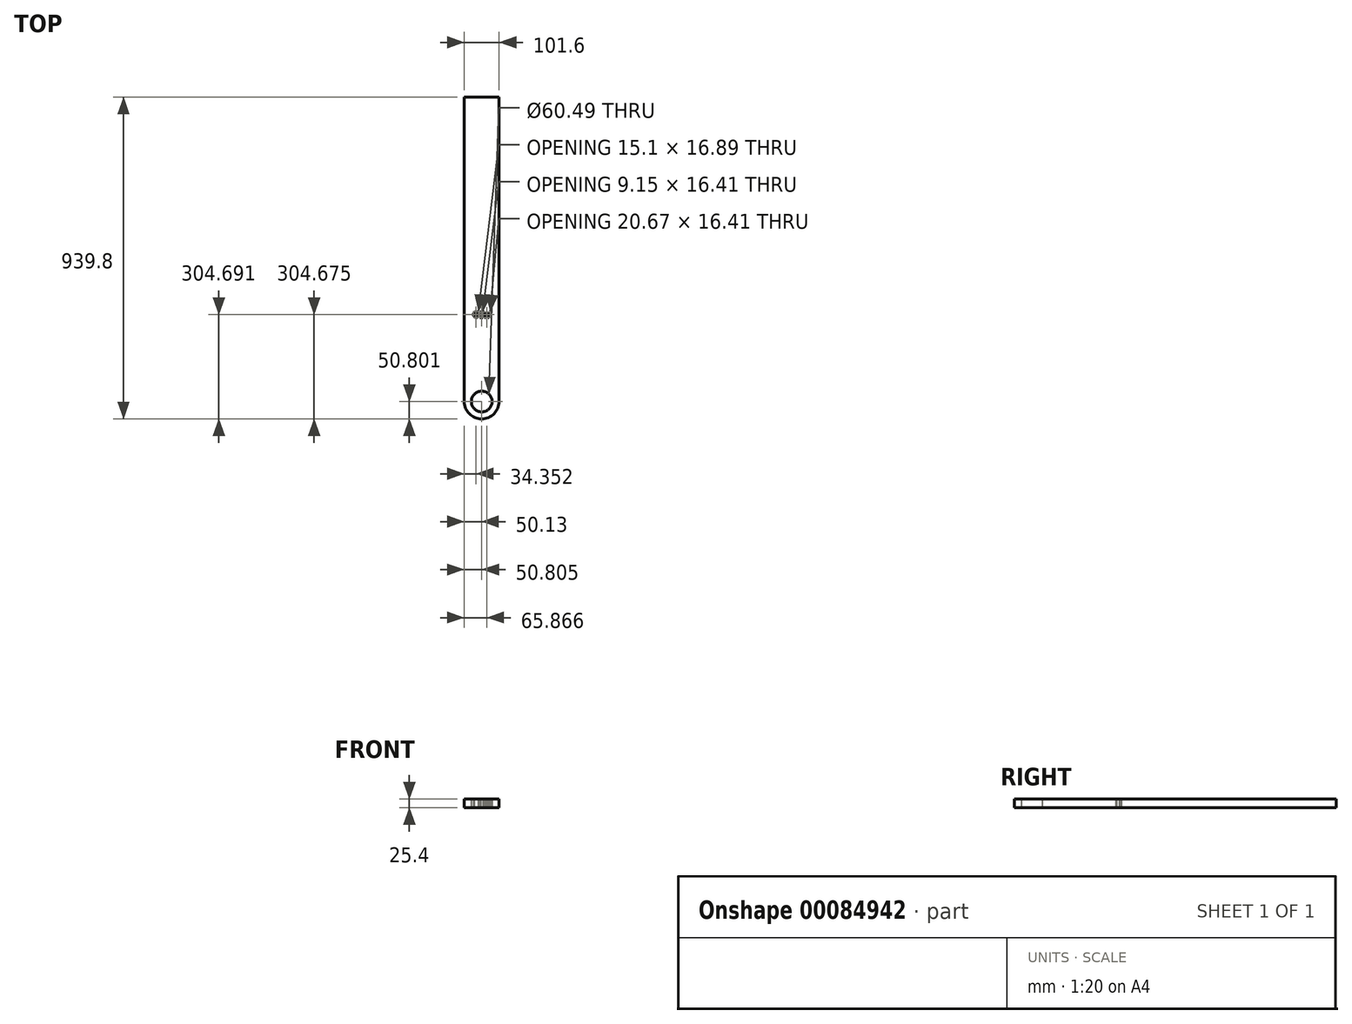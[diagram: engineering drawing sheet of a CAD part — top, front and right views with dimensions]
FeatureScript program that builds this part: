
annotation { "Feature Type Name" : "Feature", "Feature Type Description" : "" }
export const myFeature = defineFeature(function(context is Context, id is Id, definition is map)
    precondition{}
    {
        {
            var Q0;
            Q0=qCreatedBy(makeId("Top.planeOp"),FACE);
            var sketch = newSketch(context, id + "F0", { "sketchPlane" : qUnion([Q0])});
            skLineSegment(sketch, "E0", {"start": v(-88.49, -82.24) * mm, "end": v(-88.49, 806.76) * mm});
            skLineSegment(sketch, "E1", {"start": v(-88.49, 806.76) * mm, "end": v(-190.09, 806.76) * mm});
            skLineSegment(sketch, "E2", {"start": v(-190.09, 806.76) * mm, "end": v(-190.09, -82.24) * mm});
            skArc(sketch, "E3", {"start": v(-190.09, -82.24) * mm, "mid": v(-139.29, -133.04) * mm, "end": v(-88.49, -82.24) * mm});
            skCircle(sketch, "E4", {"center": v(-139.29, -82.24) * mm, "radius": 30.24 * mm});
            skLineSegment(sketch, "E5.bottom", {"start": v(-113.89, 163.43) * mm, "end": v(-164.69, 163.43) * mm});
            skLineSegment(sketch, "E5.top", {"start": v(-113.89, 713.45) * mm, "end": v(-164.69, 713.45) * mm});
            skLineSegment(sketch, "E5.left", {"start": v(-113.89, 163.43) * mm, "end": v(-113.89, 713.45) * mm});
            skLineSegment(sketch, "E5.right", {"start": v(-164.69, 163.43) * mm, "end": v(-164.69, 713.45) * mm});
            skText(sketch, "E6", { "text": "OLW", "fontName": "OpenSans-Regular.ttf"});
            const initialGuessF0  = {"E6": [-0.16469, 0.16343, 1, 0, 0.01655]};
            skSetInitialGuess(sketch, initialGuessF0);
            skSolve(sketch);
        }
        {
            var Q0;
            {var subQ3=sQuery(id+"F0.wireOp",EDGE,"E6.sketch_text.stroke-41");Q0=makeQuery(id+"F0.imprint","IMPRINT",FACE,{"disambiguationData":[TD([[makeQuery(id+"F0.imprint","IMPRINT",EDGE,{"derivedFrom":subQ3}),1.0]])]});}
            var Q1;
            {var subQ0=sQuery(id+"F0.wireOp",EDGE,"E6.sketch_text.stroke-23");Q1=makeQuery(id+"F0.imprint","IMPRINT",FACE,{"disambiguationData":[TD([[makeQuery(id+"F0.imprint","IMPRINT",EDGE,{"derivedFrom":subQ0}),1.0]])]});}
            var Q2;
            {var subQ7=sQuery(id+"F0.wireOp",EDGE,"E5.top");Q2=makeQuery(id+"F0.imprint","IMPRINT",FACE,{"disambiguationData":[TD([[makeQuery(id+"F0.imprint","IMPRINT",EDGE,{"derivedFrom":subQ7}),1.0]])]});}
            var Q3;
            Q3=makeQuery(id+"F0.imprint","IMPRINT",FACE,{"disambiguationData":[TD([[makeQuery(id+"F0.imprint","IMPRINT",EDGE,{"derivedFrom":sQuery(id+"F0.wireOp",EDGE,"E6.sketch_text.stroke-8")}),1.0]])]});
            var Q4;
            Q4=makeQuery(id+"F0.imprint","IMPRINT",FACE,{"disambiguationData":[TD([[makeQuery(id+"F0.imprint","IMPRINT",EDGE,{"derivedFrom":sQuery(id+"F0.wireOp",EDGE,"E0")}),1.0]])]});
            extrude(context, id + "F1", {"entities" : qUnion([Q0, Q1, Q2, Q3, Q4]), "depth" : 25.4 * mm});
        }
    });
